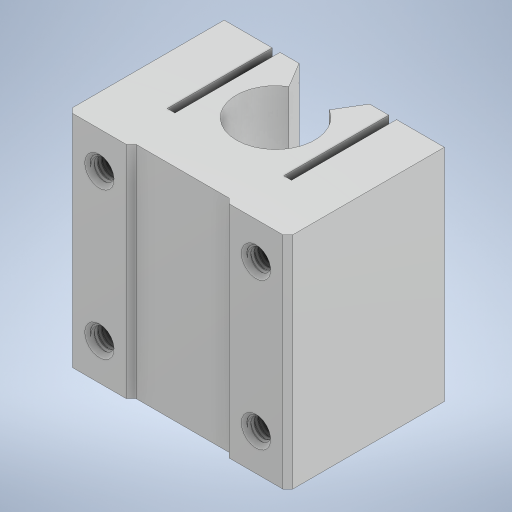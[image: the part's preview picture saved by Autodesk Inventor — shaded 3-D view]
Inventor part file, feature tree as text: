
AUTODESK INVENTOR PART (.ipt)
format: ipt  version: 2024 (Build 280153000, 153)  size: 2,504,704 bytes
history: native  units: in
note: dims shown in document units (in); Inventor stores cm internally (conversion verified against a paired STEP export)
features: extrude x4, sketch x4, projected_geometry x1, other x1
ambient origin geometry x8: Origin, YZ Plane, XZ Plane, XY Plane, X Axis, Y Axis, Z Axis, Center Point
bodies: Solid4 (feature_tree)
feature tree (10):
  extrude  "Extrusion1"  Depth=0.6299in
  extrude  "Extrusion2"  Depth=0.3937in TaperAngle=0.0deg
  extrude  "Extrusion3"  Depth=0.0625in
  extrude  "Extrusion4"  [1 undecoded]
  sketch  "Sketch1"  dims[d0=3.937in d1=0.0in d2=0.6299in]
  sketch  "Sketch2"  dims[d3=0.3937in d4=0.0in d5=0.3937in d6=0.0in]
  sketch  "Sketch3"  dims[d7=0.3937in d8=0.0in d9=0.0625in]
  projected_geometry  "Projected Loop1"
  sketch  "Sketch4"  dims[d10=0.0625in]
  other  "Guide support"
note: 1 required parameter value undecoded (feature->parameter linkage not recoverable at this tier; creation-order binding heuristic only, values carry confidence <= 0.55)
